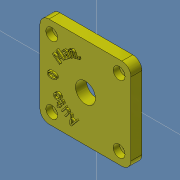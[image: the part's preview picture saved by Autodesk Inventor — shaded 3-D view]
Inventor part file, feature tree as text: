
AUTODESK INVENTOR PART (.ipt)
format: ipt  version: 2019 (Build 230136000, 136)  size: 323,584 bytes
history: native  units: mm
features: sketch x1, extrude x1, other x1, hole x1
ambient origin geometry x8: Origin, YZ Plane, XZ Plane, XY Plane, X Axis, Y Axis, Z Axis, Center Point
bodies: Volumenkörper1 (feature_tree)
feature tree (4):
  sketch  "Skizze1"  dims[d0=50.0mm d1=50.0mm d2=5.0mm d3=6.0mm d4=0.0mm d5=37.0mm d6=3.4mm d7=6.0mm d8=6.5mm d9=3.4mm d10=90.0deg d11=8.0mm d12=20.594885mm d13=11.0mm d14=30.0mm d15=1.0mm d16=0.0mm d17=15.0mm]
  extrude  "Extrusion1"  Depth=3.4mm
  other  "Prägen1"
  hole  "Bohrung1"  [1 undecoded]
note: 1 required parameter value undecoded (feature->parameter linkage not recoverable at this tier; creation-order binding heuristic only, values carry confidence <= 0.55)
